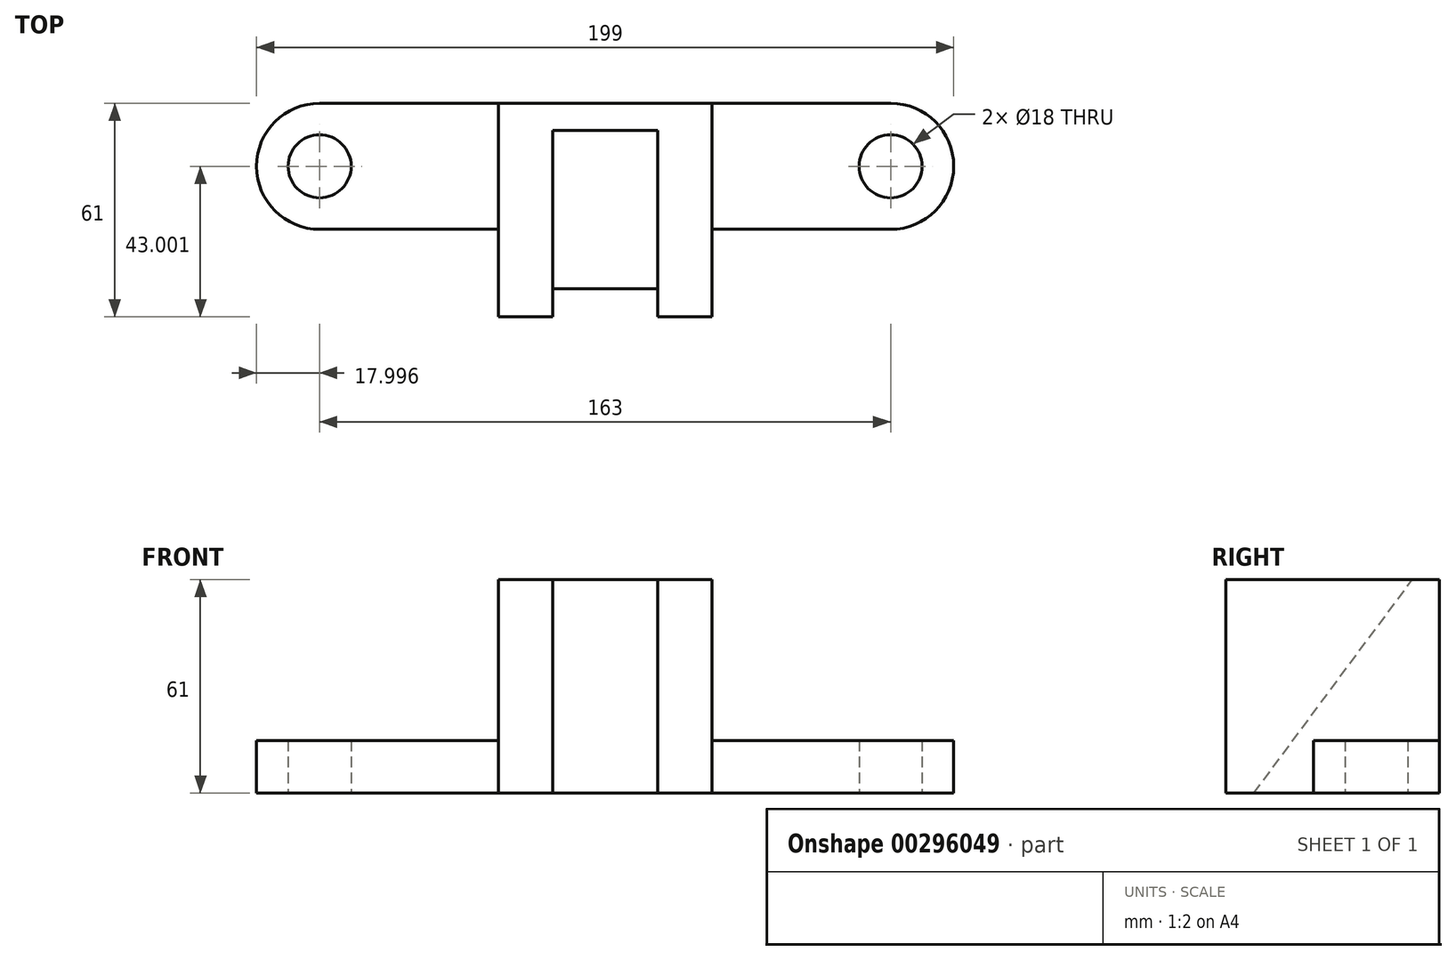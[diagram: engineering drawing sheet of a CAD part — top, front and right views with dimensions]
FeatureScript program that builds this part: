
annotation { "Feature Type Name" : "Feature", "Feature Type Description" : "" }
export const myFeature = defineFeature(function(context is Context, id is Id, definition is map)
    precondition{}
    {
        {
            var Q0;
            Q0=qCreatedBy(makeId("Top.planeOp"),FACE);
            var sketch = newSketch(context, id + "F0", { "sketchPlane" : qUnion([Q0])});
            skLineSegment(sketch, "E0", {"start": v(-2.16, -13.95) * mm, "end": v(-2.16, 47.05) * mm});
            skLineSegment(sketch, "E1", {"start": v(-2.16, 47.05) * mm, "end": v(58.84, 47.05) * mm});
            skLineSegment(sketch, "E2", {"start": v(58.84, 47.05) * mm, "end": v(58.84, -13.95) * mm});
            skLineSegment(sketch, "E3", {"start": v(58.84, -13.95) * mm, "end": v(43.34, -13.95) * mm});
            skPoint(sketch, "E4.orphan", {"position": v(-2.16, -19.38) * mm});
            skLineSegment(sketch, "E5", {"start": v(13.34, -13.95) * mm, "end": v(13.34, 39.3) * mm});
            skLineSegment(sketch, "E6", {"start": v(13.34, 39.3) * mm, "end": v(43.34, 39.3) * mm});
            skLineSegment(sketch, "E7", {"start": v(43.34, 39.3) * mm, "end": v(43.34, -13.95) * mm});
            skLineSegment(sketch, "E8.trimOffspring", {"start": v(13.34, -13.95) * mm, "end": v(-2.16, -13.95) * mm});
            skLineSegment(sketch, "E9", {"start": v(58.84, 47.05) * mm, "end": v(109.84, 47.05) * mm});
            skLineSegment(sketch, "E10", {"start": v(-2.16, 47.05) * mm, "end": v(-53.16, 47.05) * mm});
            skLineSegment(sketch, "E11", {"start": v(-53.16, 47.05) * mm, "end": v(-53.16, 11.05) * mm, "construction": true});
            skLineSegment(sketch, "E12", {"start": v(109.84, 29.05) * mm, "end": v(109.84, 11.05) * mm, "construction": true});
            skLineSegment(sketch, "E13", {"start": v(109.84, 11.05) * mm, "end": v(58.84, 11.05) * mm});
            skLineSegment(sketch, "E14", {"start": v(-53.16, 11.05) * mm, "end": v(-2.16, 11.05) * mm});
            skLineSegment(sketch, "E15", {"start": v(109.84, 47.05) * mm, "end": v(109.84, 29.05) * mm, "construction": true});
            skLineSegment(sketch, "E16", {"start": v(109.84, 29.05) * mm, "end": v(58.84, 29.05) * mm, "construction": true});
            skArc(sketch, "E17", {"start": v(109.84, 11.05) * mm, "mid": v(127.84, 29.05) * mm, "end": v(109.84, 47.05) * mm});
            skCircle(sketch, "E18", {"center": v(109.84, 29.05) * mm, "radius": 9 * mm});
            skLineSegment(sketch, "E19", {"start": v(28.34, 47.05) * mm, "end": v(28.34, -30.23) * mm, "construction": true});
            skArc(sketch, "E20.MirrorCS", {"start": v(-53.16, 11.05) * mm, "mid": v(-71.16, 29.05) * mm, "end": v(-53.16, 47.05) * mm});
            skCircle(sketch, "E21.MirrorC", {"center": v(-53.16, 29.05) * mm, "radius": 9 * mm});
            skSolve(sketch);
        }
        {
            var Q0;
            Q0=makeQuery(id+"F0.imprint","IMPRINT",FACE,{"disambiguationData":[TD([[makeQuery(id+"F0.imprint","IMPRINT",EDGE,{"derivedFrom":sQuery(id+"F0.wireOp",EDGE,"E0")}),-1.0]])]});
            extrude(context, id + "F1", {"entities" : qUnion([Q0]), "depth" : 61 * mm});
        }
        {
            var Q0;
            Q0=makeQuery(id+"F1.opExtrude","SWEPT_FACE",FACE,{"disambiguationData":[OSD([sQuery(id+"F0.wireOp",EDGE,"E7")])]});
            var sketch = newSketch(context, id + "F2", { "sketchPlane" : qUnion([Q0])});
            skLineSegment(sketch, "E22", {"start": v(5.95, 0) * mm, "end": v(-39.3, 61) * mm});
            skLineSegment(sketch, "E23", {"start": v(-39.3, 61) * mm, "end": v(-39.3, 0) * mm});
            skLineSegment(sketch, "E24", {"start": v(-39.3, 0) * mm, "end": v(5.95, 0) * mm});
            skSolve(sketch);
        }
        {
            var Q0;
            Q0=makeQuery(id+"F2.imprint","IMPRINT",FACE,{"disambiguationData":[TD([[makeQuery(id+"F2.imprint","IMPRINT",EDGE,{"derivedFrom":sQuery(id+"F2.wireOp",EDGE,"E22")}),1.0]])]});
            extrude(context, id + "F3", {"entities" : qUnion([Q0]), "operationType" : NewBodyOperationType.ADD, "depth" : 30 * mm});
        }
        {
            var Q0;
            {var subQ1=sQuery(id+"F0.wireOp",EDGE,"E10");Q0=makeQuery(id+"F0.imprint","IMPRINT",FACE,{"disambiguationData":[TD([[makeQuery(id+"F0.imprint","IMPRINT",EDGE,{"derivedFrom":subQ1}),1.0]])]});}
            var Q1;
            {var subQ0=sQuery(id+"F0.wireOp",EDGE,"E9");Q1=makeQuery(id+"F0.imprint","IMPRINT",FACE,{"disambiguationData":[TD([[makeQuery(id+"F0.imprint","IMPRINT",EDGE,{"derivedFrom":subQ0}),-1.0]])]});}
            extrude(context, id + "F4", {"entities" : qUnion([Q0, Q1]), "operationType" : NewBodyOperationType.ADD, "depth" : 15 * mm});
        }
    });
